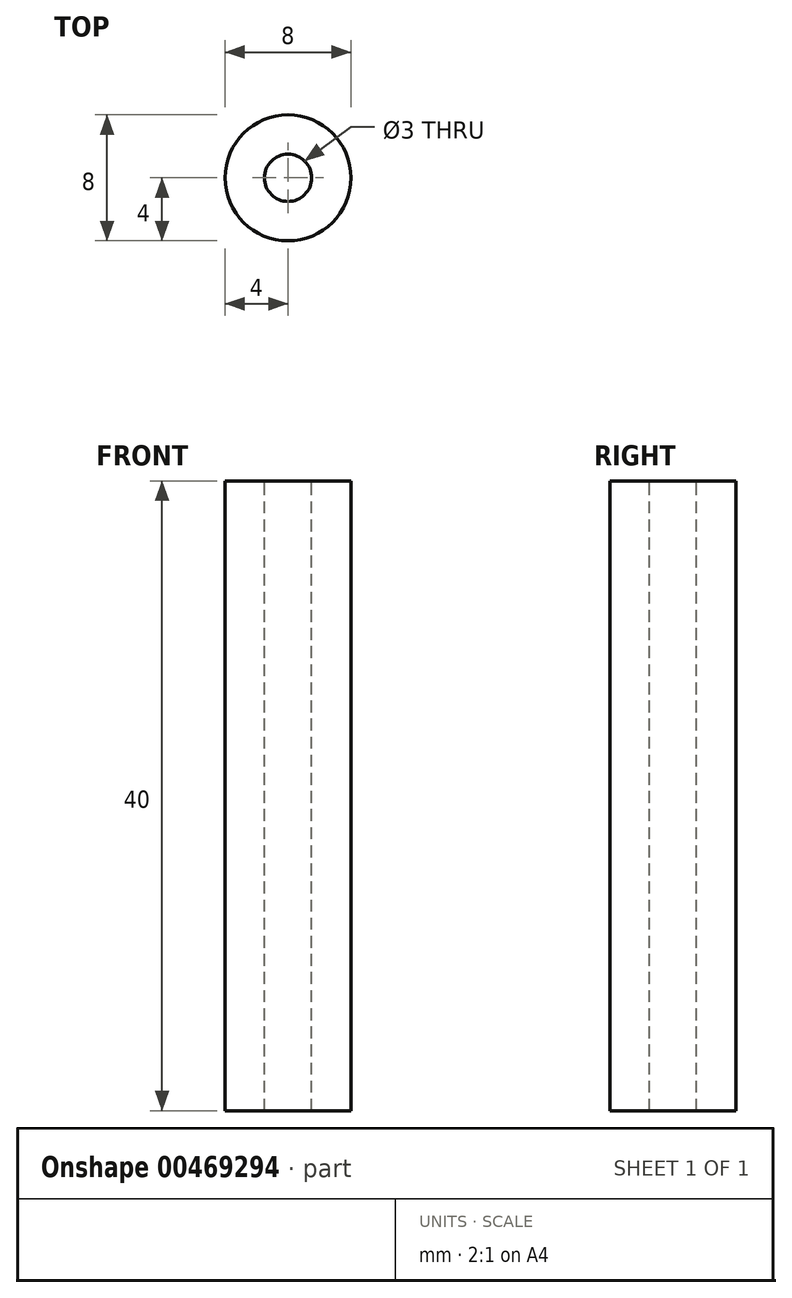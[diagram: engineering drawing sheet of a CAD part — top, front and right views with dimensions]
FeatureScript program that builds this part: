
annotation { "Feature Type Name" : "Feature", "Feature Type Description" : "" }
export const myFeature = defineFeature(function(context is Context, id is Id, definition is map)
    precondition{}
    {
        {
            var Q0;
            Q0=qCreatedBy(makeId("Top.planeOp"),FACE);
            var sketch = newSketch(context, id + "F0", { "sketchPlane" : qUnion([Q0])});
            skCircle(sketch, "E0", {"center": v(0, 0) * mm, "radius": 4 * mm});
            skSolve(sketch);
        }
        {
            var Q0;
            Q0 = qSketchRegion(id + "F0", true);
            extrude(context, id + "F1", {"entities" : qUnion([Q0]), "depth" : 40 * mm, "offsetDistance" : 25 * mm});
        }
        {
            var Q0;
            Q0=makeQuery(id+"F1.opExtrude","CAP_FACE",FACE,{"disambiguationData":[OSD([sQuery(id+"F0.wireOp",EDGE,"E0")])],"isStart":false});
            var sketch = newSketch(context, id + "F2", { "sketchPlane" : qUnion([Q0])});
            skPoint(sketch, "E1", {"position": v(0, 0) * mm});
            skSolve(sketch);
        }
        {
            var Q0;
            Q0=sQuery(id+"F2.wireOp",VERTEX,"E1");
            var Q1;
            Q1=makeQuery(id+"F1.opExtrude","SWEPT_BODY",BODY,{"disambiguationData":[OSD([sQuery(id+"F0.wireOp",EDGE,"E0")])]});
            hole(context, id + "F3", {"style" : HoleStyle.SIMPLE, "endStyle" : HoleEndStyle.THROUGH, "holeDiameter" : 3 * mm, "isTappedThrough" : true, "tappedDepth" : 12 * mm, "tapClearance" : 3, "locations" : qUnion([Q0]), "scope" : qUnion([Q1])});
        }
    });
